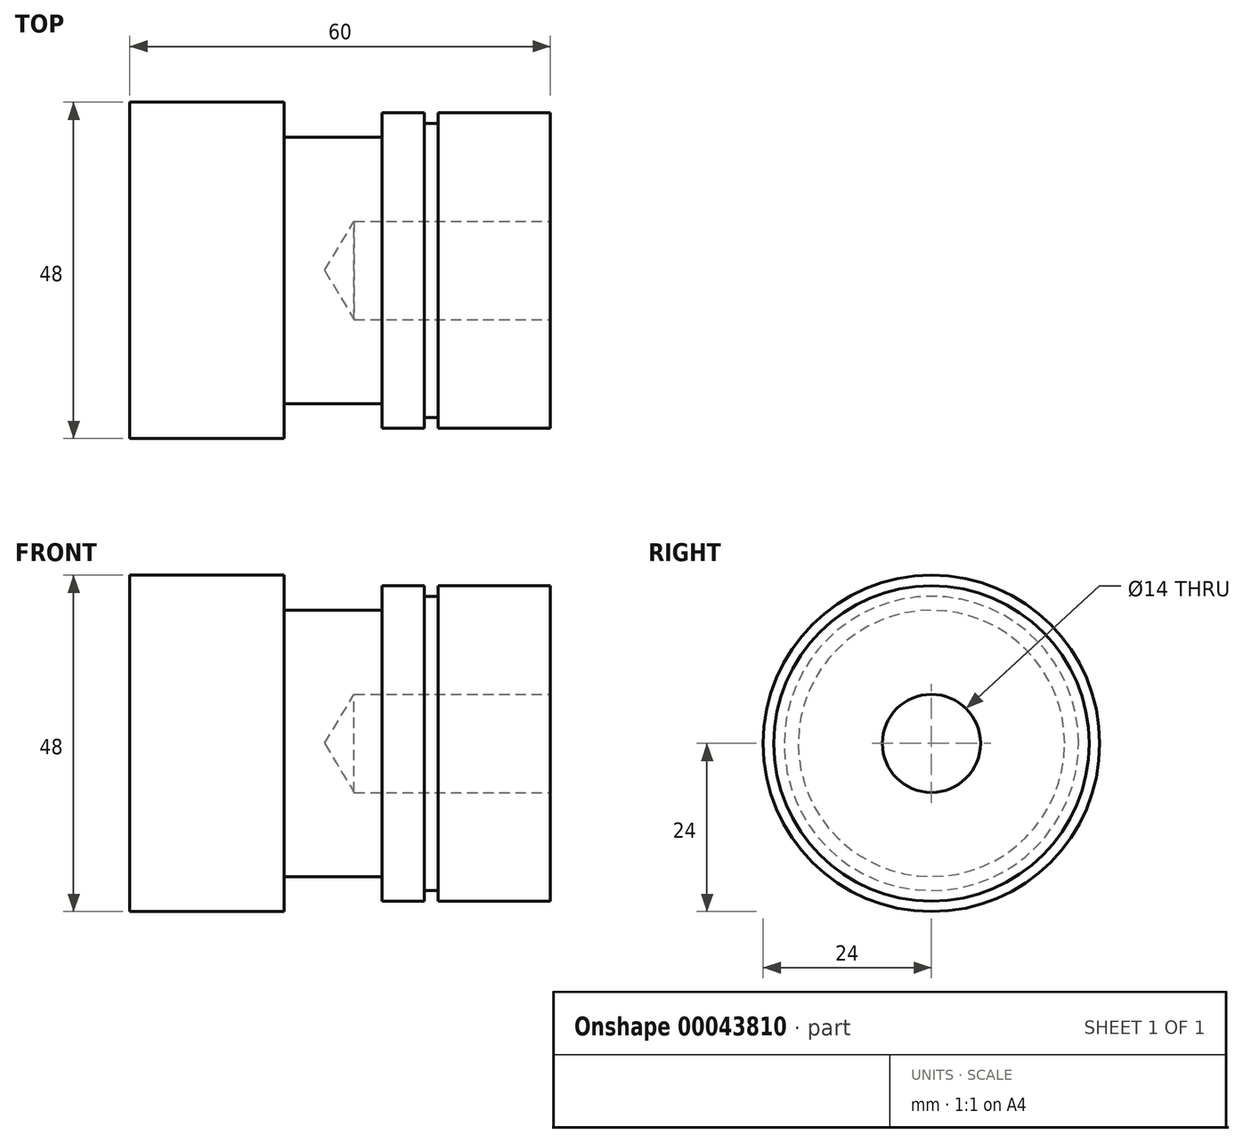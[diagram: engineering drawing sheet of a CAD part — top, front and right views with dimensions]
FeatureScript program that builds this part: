
annotation { "Feature Type Name" : "Feature", "Feature Type Description" : "" }
export const myFeature = defineFeature(function(context is Context, id is Id, definition is map)
    precondition{}
    {
        {
            var Q0;
            Q0=qCreatedBy(makeId("Front.planeOp"),FACE);
            var sketch = newSketch(context, id + "F0", { "sketchPlane" : qUnion([Q0])});
            skLineSegment(sketch, "E0", {"start": v(0, 0) * mm, "end": v(0, 24) * mm});
            skLineSegment(sketch, "E1", {"start": v(0, 24) * mm, "end": v(22, 24) * mm});
            skLineSegment(sketch, "E2", {"start": v(22, 24) * mm, "end": v(22, 19) * mm});
            skLineSegment(sketch, "E3", {"start": v(22, 19) * mm, "end": v(36, 19) * mm});
            skLineSegment(sketch, "E4", {"start": v(36, 19) * mm, "end": v(36, 22.5) * mm});
            skLineSegment(sketch, "E5", {"start": v(36, 22.5) * mm, "end": v(42, 22.5) * mm});
            skLineSegment(sketch, "E6", {"start": v(42, 22.5) * mm, "end": v(42, 21) * mm});
            skLineSegment(sketch, "E7", {"start": v(42, 21) * mm, "end": v(44, 21) * mm});
            skLineSegment(sketch, "E8", {"start": v(44, 21) * mm, "end": v(44, 22.5) * mm});
            skLineSegment(sketch, "E9", {"start": v(44, 22.5) * mm, "end": v(60, 22.5) * mm});
            skLineSegment(sketch, "E10", {"start": v(60, 22.5) * mm, "end": v(60, 0) * mm});
            skLineSegment(sketch, "E11", {"start": v(60, 0) * mm, "end": v(0, 0) * mm});
            skSolve(sketch);
        }
        {
            var Q0;
            Q0=makeQuery(id+"F0.imprint","IMPRINT",FACE,{"disambiguationData":[TD([[makeQuery(id+"F0.imprint","IMPRINT",EDGE,{"derivedFrom":sQuery(id+"F0.wireOp",EDGE,"E0")}),-1.0]])]});
            var Q1;
            Q1=sQuery(id+"F0.wireOp",EDGE,"E11");
            revolve(context, id + "F1", {"entities" : qUnion([Q0]), "axis" : qUnion([Q1]), "revolveType" : RevolveType.FULL});
        }
        {
            var Q0;
            Q0=makeQuery(id+"F1.opRevolve","SWEPT_FACE",FACE,{"disambiguationData":[OSD([sQuery(id+"F0.wireOp",EDGE,"E10")])]});
            var sketch = newSketch(context, id + "F2", { "sketchPlane" : qUnion([Q0])});
            skLineSegment(sketch, "E12", {"start": v(0, 0) * mm, "end": v(0, 11.27) * mm});
            skSolve(sketch);
        }
        {
            var Q0;
            Q0=sQuery(id+"F2.wireOp",VERTEX,"E12.start");
            var Q1;
            Q1=makeQuery(id+"F1.opRevolve","SWEPT_BODY",BODY,{"disambiguationData":[OSD([sQuery(id+"F0.wireOp",EDGE,"E0"),sQuery(id+"F0.wireOp",EDGE,"E1"),sQuery(id+"F0.wireOp",EDGE,"E2"),sQuery(id+"F0.wireOp",EDGE,"E3"),sQuery(id+"F0.wireOp",EDGE,"E4"),sQuery(id+"F0.wireOp",EDGE,"E5"),sQuery(id+"F0.wireOp",EDGE,"E6"),sQuery(id+"F0.wireOp",EDGE,"E7"),sQuery(id+"F0.wireOp",EDGE,"E8"),sQuery(id+"F0.wireOp",EDGE,"E9"),sQuery(id+"F0.wireOp",EDGE,"E10"),sQuery(id+"F0.wireOp",EDGE,"E11")])]});
            hole(context, id + "F3", {"style" : HoleStyle.SIMPLE, "holeDiameter" : 14 * mm, "endStyle" : HoleEndStyle.BLIND, "holeDepth" : 28 * mm, "locations" : qUnion([Q0]), "scope" : qUnion([Q1])});
        }
    });
